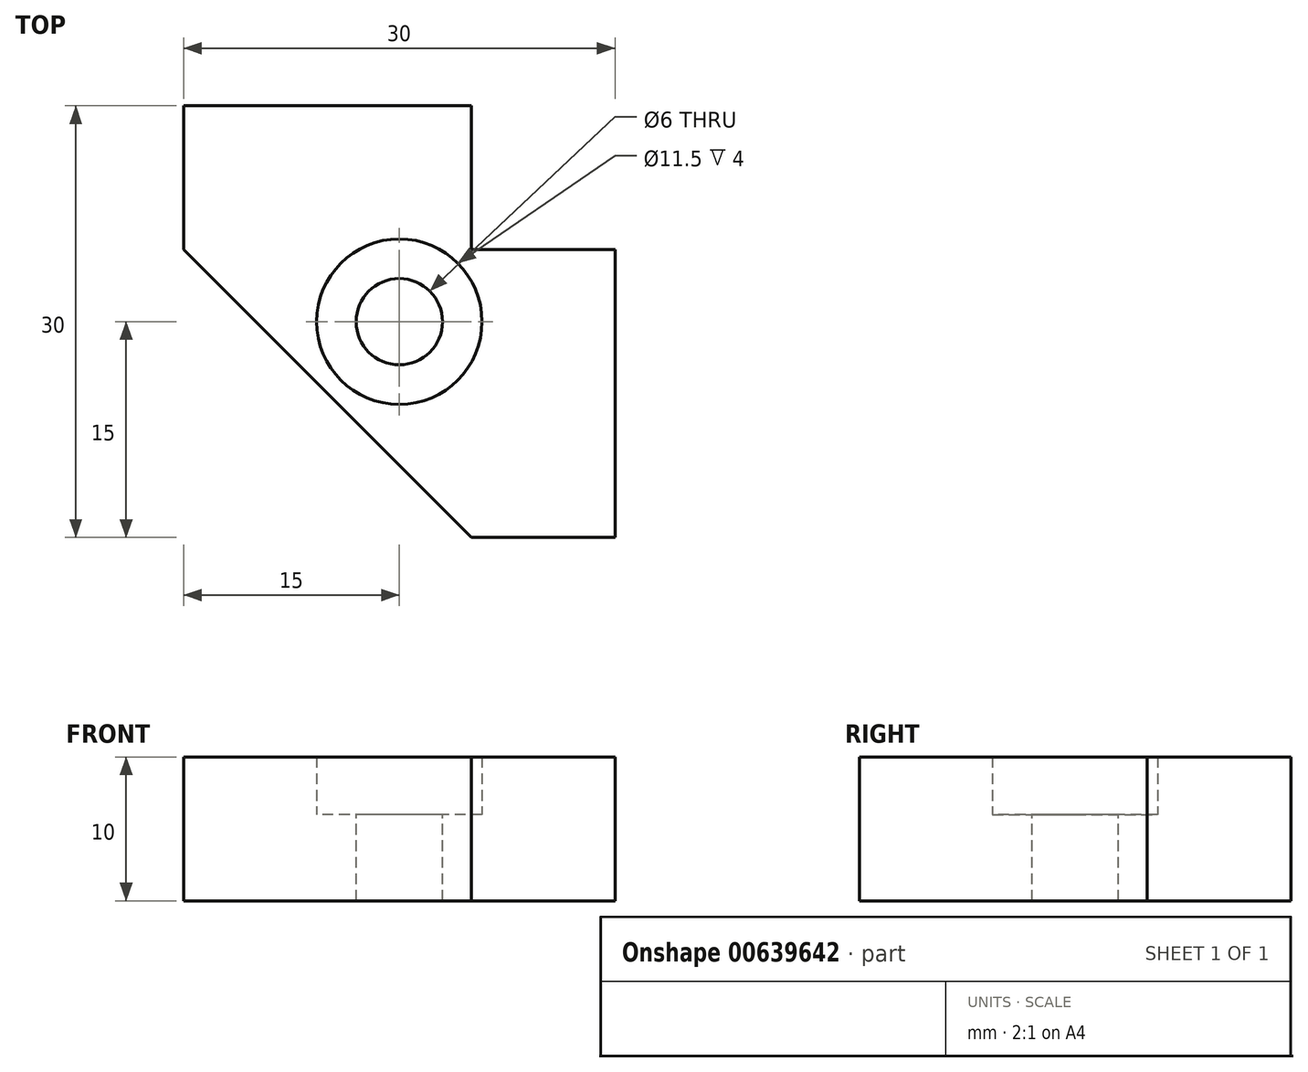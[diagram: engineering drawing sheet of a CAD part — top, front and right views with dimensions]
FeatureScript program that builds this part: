
annotation { "Feature Type Name" : "Feature", "Feature Type Description" : "" }
export const myFeature = defineFeature(function(context is Context, id is Id, definition is map)
    precondition{}
    {
        {
            var Q0;
            Q0=qCreatedBy(makeId("Top.planeOp"),FACE);
            var sketch = newSketch(context, id + "F0", { "sketchPlane" : qUnion([Q0])});
            skLineSegment(sketch, "E0", {"start": v(0, 0) * mm, "end": v(0, -20) * mm});
            skLineSegment(sketch, "E1", {"start": v(0, 0) * mm, "end": v(-20, 0) * mm});
            skLineSegment(sketch, "E2", {"start": v(-20, 0) * mm, "end": v(0, -20) * mm});
            skSolve(sketch);
        }
        {
            var Q0;
            Q0=makeQuery(id+"F0.imprint","IMPRINT",FACE,{"disambiguationData":[TD([[makeQuery(id+"F0.imprint","IMPRINT",EDGE,{"derivedFrom":sQuery(id+"F0.wireOp",EDGE,"E0")}),-1.0]])]});
            extrude(context, id + "F1", {"entities" : qUnion([Q0]), "depth" : 6 * mm, "offsetDistance" : 25 * mm});
        }
        {
            var Q0;
            Q0=qCreatedBy(makeId("Front.planeOp"),FACE);
            var sketch = newSketch(context, id + "F2", { "sketchPlane" : qUnion([Q0])});
            skSolve(sketch);
        }
        {
            var Q0;
            Q0 = qSketchRegion(id + "F2", true);
            var Q1;
            Q1=makeQuery(id+"F1.opExtrude","SWEPT_FACE",FACE,{"disambiguationData":[OSD([sQuery(id+"F0.wireOp",EDGE,"E1")])]});
            extrude(context, id + "F3", {"entities" : qUnion([Q0, Q1]), "operationType" : NewBodyOperationType.ADD, "depth" : 10 * mm, "offsetDistance" : 25 * mm});
        }
        {
            var Q0;
            {var subQ0=sQuery(id+"F0.wireOp",EDGE,"E0");Q0=makeQuery(id+"F3.boolean.opBoolean","MERGE",FACE,{"derivedFrom":[makeQuery(id+"F1.opExtrude","SWEPT_FACE",FACE,{"disambiguationData":[OSD([subQ0])]}),makeQuery(id+"F3.opExtrude","SWEPT_FACE",FACE,{"disambiguationData":[OSD([subQ0,sQuery(id+"F0.wireOp",EDGE,"E1")])]})]});}
            var sketch = newSketch(context, id + "F4", { "sketchPlane" : qUnion([Q0])});
            skLineSegment(sketch, "E3.bottom", {"start": v(0, 0) * mm, "end": v(-20, 0) * mm});
            skLineSegment(sketch, "E3.top", {"start": v(0, 6) * mm, "end": v(-20, 6) * mm});
            skLineSegment(sketch, "E3.left", {"start": v(0, 0) * mm, "end": v(0, 6) * mm});
            skLineSegment(sketch, "E3.right", {"start": v(-20, 0) * mm, "end": v(-20, 6) * mm});
            skSolve(sketch);
        }
        {
            var Q0;
            Q0=makeQuery(id+"F4.imprint","IMPRINT",FACE,{"disambiguationData":[TD([[makeQuery(id+"F4.imprint","IMPRINT",EDGE,{"derivedFrom":sQuery(id+"F4.wireOp",EDGE,"E3.bottom")}),-1.0]])]});
            extrude(context, id + "F5", {"entities" : qUnion([Q0]), "operationType" : NewBodyOperationType.ADD, "depth" : 10 * mm, "offsetDistance" : 25 * mm});
        }
        {
            var Q0;
            {var subQ0=sQuery(id+"F0.wireOp",EDGE,"E1");Q0=makeQuery(id+"F5.boolean.opBoolean","MERGE",FACE,{"derivedFrom":[makeQuery(id+"F3.boolean.opBoolean","MERGE",FACE,{"derivedFrom":[makeQuery(id+"F1.opExtrude","CAP_FACE",FACE,{"disambiguationData":[OSD([sQuery(id+"F0.wireOp",EDGE,"E0"),subQ0,sQuery(id+"F0.wireOp",EDGE,"E2")])],"isStart":false}),makeQuery(id+"F3.opExtrude","SWEPT_FACE",FACE,{"disambiguationData":[OSD([subQ0]),TDD([makeQuery(id+"F1.opExtrude","CAP_EDGE",EDGE,{"disambiguationData":[OSD([subQ0])],"isStart":false})])]})]}),makeQuery(id+"F5.opExtrude","SWEPT_FACE",FACE,{"disambiguationData":[OSD([sQuery(id+"F4.wireOp",EDGE,"E3.top")])]})]});}
            var sketch = newSketch(context, id + "F6", { "sketchPlane" : qUnion([Q0])});
            skLineSegment(sketch, "E4", {"start": v(-5, -5) * mm, "end": v(-10, -10) * mm});
            skCircle(sketch, "E5", {"center": v(-5, -5) * mm, "radius": 5.75 * mm});
            skCircle(sketch, "E6", {"center": v(-5, -5) * mm, "radius": 3 * mm});
            skSolve(sketch);
        }
        {
            var Q0;
            Q0=makeQuery(id+"F6.imprint","IMPRINT",FACE,{"disambiguationData":[TD([[makeQuery(id+"F6.imprint","IMPRINT",EDGE,{"derivedFrom":sQuery(id+"F6.wireOp",EDGE,"E6")}),1.0]])]});
            extrude(context, id + "F7", {"entities" : qUnion([Q0]), "operationType" : NewBodyOperationType.REMOVE, "oppositeDirection" : true, "depth" : 25 * mm, "offsetDistance" : 25 * mm});
        }
        {
            var Q0;
            Q0=makeQuery(id+"F6.imprint","IMPRINT",FACE,{"disambiguationData":[TD([[makeQuery(id+"F6.imprint","IMPRINT",EDGE,{"derivedFrom":sQuery(id+"F6.wireOp",EDGE,"E5")}),-1.0]])]});
            extrude(context, id + "F8", {"entities" : qUnion([Q0]), "operationType" : NewBodyOperationType.ADD, "depth" : 4 * mm, "offsetDistance" : 25 * mm});
        }
    });
